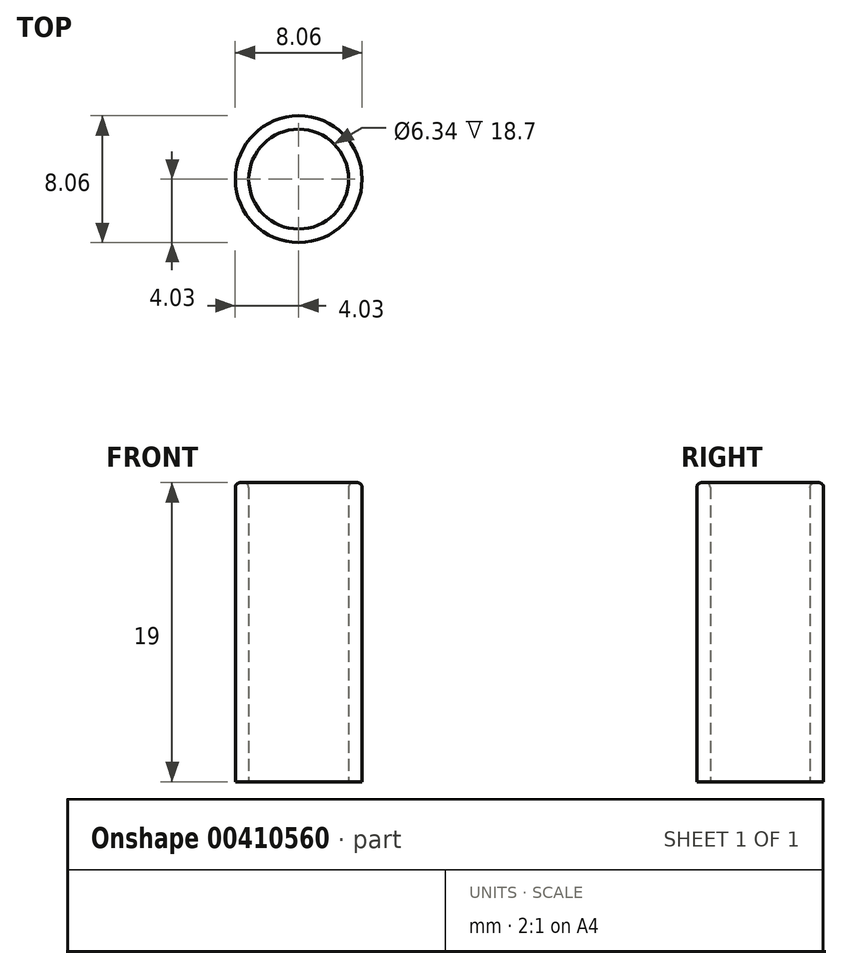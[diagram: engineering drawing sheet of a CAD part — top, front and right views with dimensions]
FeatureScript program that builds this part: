
annotation { "Feature Type Name" : "Feature", "Feature Type Description" : "" }
export const myFeature = defineFeature(function(context is Context, id is Id, definition is map)
    precondition{}
    {
        {
            var Q0;
            Q0=qCreatedBy(makeId("Top.planeOp"),FACE);
            var sketch = newSketch(context, id + "F0", { "sketchPlane" : qUnion([Q0])});
            skCircle(sketch, "E0", {"center": v(0, 0) * mm, "radius": 4.03 * mm});
            skCircle(sketch, "E1", {"center": v(0, 0) * mm, "radius": 3.17 * mm});
            skSolve(sketch);
        }
        {
            var Q0;
            Q0=makeQuery(id+"F0.imprint","IMPRINT",FACE,{"disambiguationData":[TD([[makeQuery(id+"F0.imprint","IMPRINT",EDGE,{"derivedFrom":sQuery(id+"F0.wireOp",EDGE,"E0")}),1.0]])]});
            extrude(context, id + "F1", {"entities" : qUnion([Q0]), "depth" : 19 * mm});
        }
        {
            var Q0;
            Q0=makeQuery(id+"F1.opExtrude","CAP_EDGE",EDGE,{"disambiguationData":[OSD([sQuery(id+"F0.wireOp",EDGE,"E0")])],"isStart":false});
            var Q1;
            Q1=makeQuery(id+"F1.opExtrude","CAP_EDGE",EDGE,{"disambiguationData":[OSD([sQuery(id+"F0.wireOp",EDGE,"E1")])],"isStart":false});
            fillet(context, id + "F2", {"entities" : qUnion([Q0, Q1]), "radius" : .3 * mm, "tangentPropagation" : true, "allowEdgeOverflow" : false});
        }
    });
